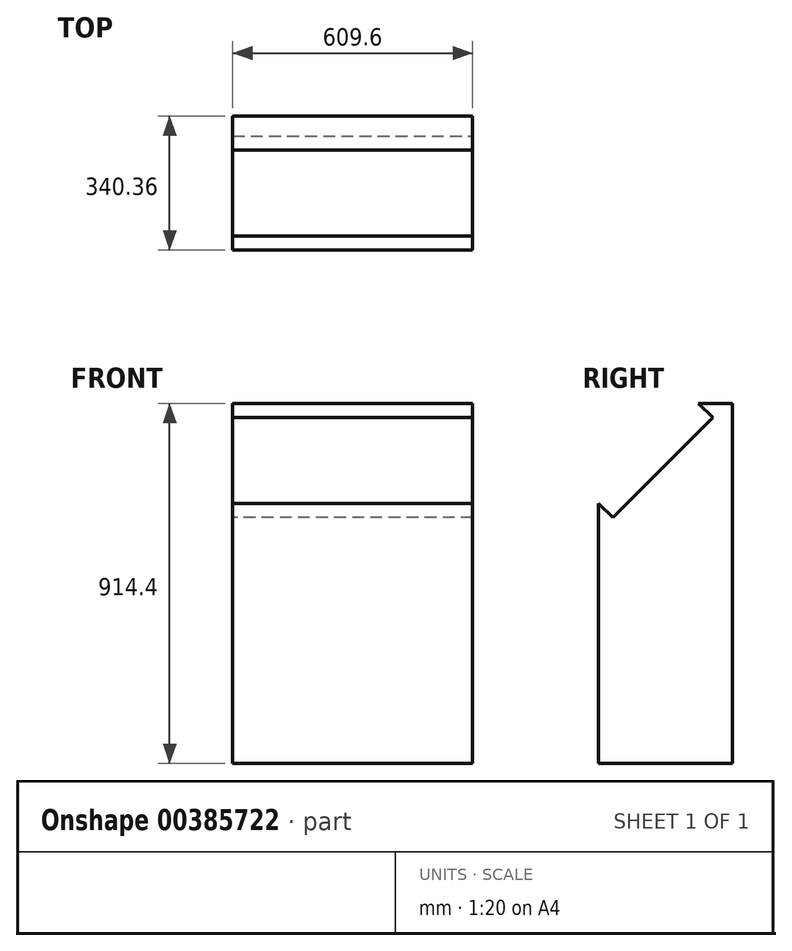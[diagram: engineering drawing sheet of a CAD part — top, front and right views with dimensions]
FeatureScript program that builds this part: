
annotation { "Feature Type Name" : "Feature", "Feature Type Description" : "" }
export const myFeature = defineFeature(function(context is Context, id is Id, definition is map)
    precondition{}
    {
        {
            var Q0;
            Q0=qCreatedBy(makeId("Front.planeOp"),FACE);
            var sketch = newSketch(context, id + "F0", { "sketchPlane" : qUnion([Q0])});
            skLineSegment(sketch, "E0.bottom", {"start": v(-304.8, 457.2) * mm, "end": v(304.8, 457.2) * mm});
            skLineSegment(sketch, "E0.top", {"start": v(-304.8, -457.2) * mm, "end": v(304.8, -457.2) * mm});
            skLineSegment(sketch, "E0.left", {"start": v(-304.8, 457.2) * mm, "end": v(-304.8, -457.2) * mm});
            skLineSegment(sketch, "E0.right", {"start": v(304.8, 457.2) * mm, "end": v(304.8, -457.2) * mm});
            skPoint(sketch, "E0.middle", {"position": v(0, 0) * mm});
            skSolve(sketch);
        }
        {
            var Q0;
            Q0 = qSketchRegion(id + "F0", true);
            extrude(context, id + "F1", {"entities" : qUnion([Q0]), "depth" : 340.36 * mm});
        }
        {
            var Q0;
            Q0=makeQuery(id+"F1.opExtrude","CAP_EDGE",EDGE,{"disambiguationData":[OSD([sQuery(id+"F0.wireOp",EDGE,"E0.bottom")])],"isStart":false});
            chamfer(context, id + "F2", {"entities" : qUnion([Q0]), "width" : 254 * mm, "tangentPropagation" : true});
        }
        {
            var Q0;
            Q0=makeQuery(id+"F2.opChamfer","BLEND_FACE",FACE,{"disambiguationData":[OSD([sQuery(id+"F0.wireOp",EDGE,"E0.bottom")])]});
            extrude(context, id + "F3", {"entities" : qUnion([Q0]), "operationType" : NewBodyOperationType.REMOVE, "oppositeDirection" : true, "depth" : 50.8 * mm});
        }
    });
